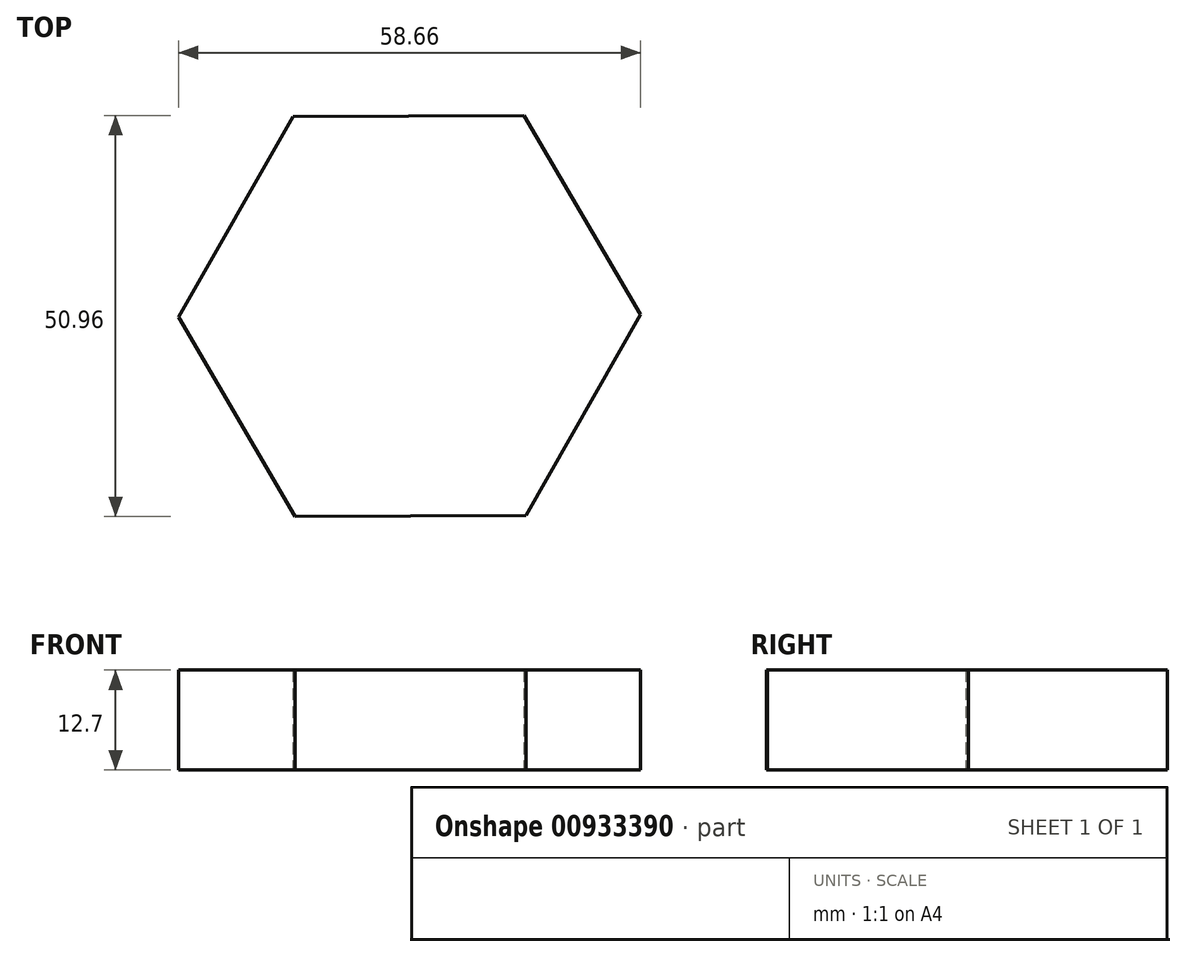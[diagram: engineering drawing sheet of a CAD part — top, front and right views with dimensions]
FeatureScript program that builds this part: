
annotation { "Feature Type Name" : "Feature", "Feature Type Description" : "" }
export const myFeature = defineFeature(function(context is Context, id is Id, definition is map)
    precondition{}
    {
        {
            var Q0;
            Q0=qCreatedBy(makeId("Top.planeOp"),FACE);
            var sketch = newSketch(context, id + "F0", { "sketchPlane" : qUnion([Q0])});
            skCircle(sketch, "E0.cCircle", {"center": v(0, 0) * mm, "radius": 25.4 * mm, "construction": true});
            skLineSegment(sketch, "E0.0", {"start": v(29.33, 0.16) * mm, "end": v(14.8, -25.32) * mm});
            skLineSegment(sketch, "E0.1", {"start": v(14.8, -25.32) * mm, "end": v(-14.53, -25.48) * mm});
            skLineSegment(sketch, "E0.2", {"start": v(-14.53, -25.48) * mm, "end": v(-29.33, -0.16) * mm});
            skLineSegment(sketch, "E0.3", {"start": v(-29.33, -0.16) * mm, "end": v(-14.8, 25.32) * mm});
            skLineSegment(sketch, "E0.4", {"start": v(-14.8, 25.32) * mm, "end": v(14.53, 25.48) * mm});
            skLineSegment(sketch, "E0.5", {"start": v(14.53, 25.48) * mm, "end": v(29.33, 0.16) * mm});
            skPoint(sketch, "E0.0.midPoint", {"position": v(22.07, -12.58) * mm});
            skSolve(sketch);
        }
        {
            var Q0;
            Q0 = qSketchRegion(id + "F0", true);
            extrude(context, id + "F1", {"entities" : qUnion([Q0]), "depth" : 12.7 * mm, "offsetDistance" : 25.4 * mm});
        }
    });
